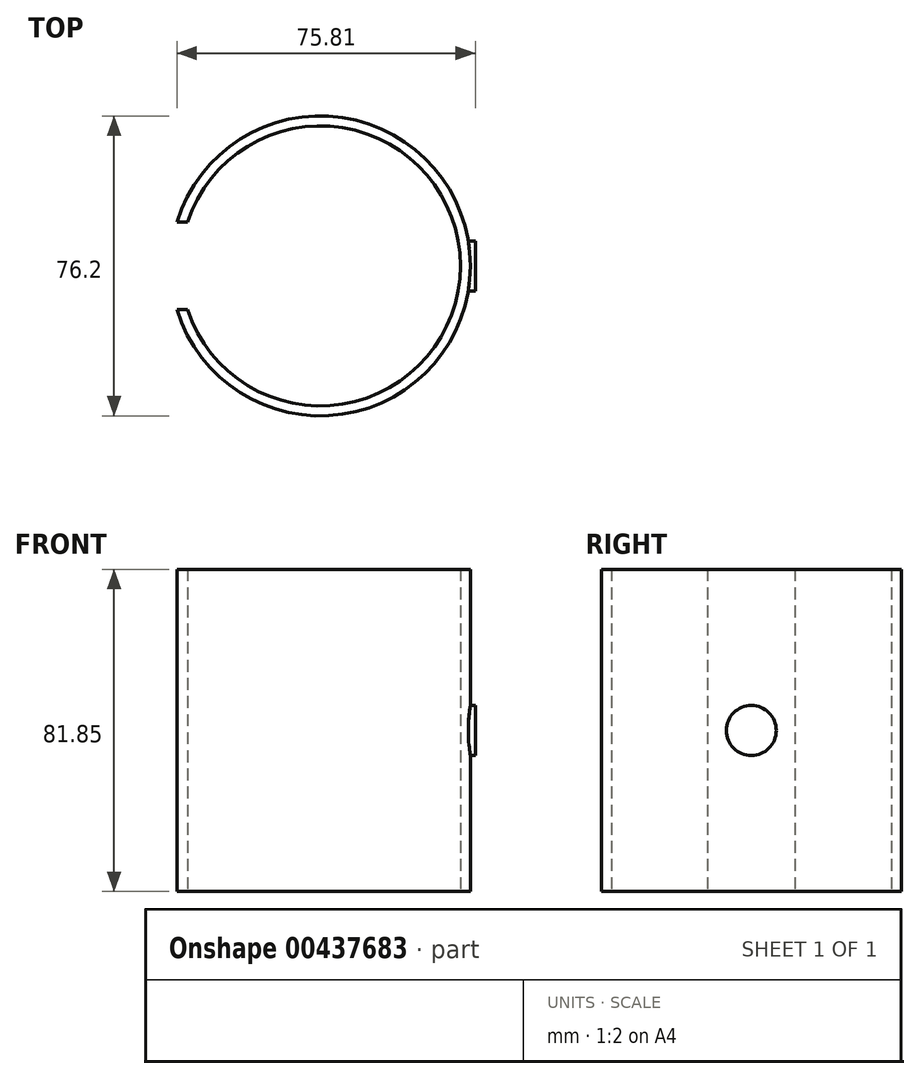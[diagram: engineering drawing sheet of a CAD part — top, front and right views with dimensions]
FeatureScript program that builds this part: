
annotation { "Feature Type Name" : "Feature", "Feature Type Description" : "" }
export const myFeature = defineFeature(function(context is Context, id is Id, definition is map)
    precondition{}
    {
        {
            var Q0;
            Q0=qCreatedBy(makeId("Top.planeOp"),FACE);
            var sketch = newSketch(context, id + "F0", { "sketchPlane" : qUnion([Q0])});
            skCircle(sketch, "E0", {"center": v(0, 0) * mm, "radius": 38.1 * mm});
            skLineSegment(sketch, "E1.bottom", {"start": v(-36.44, 11.1) * mm, "end": v(36.44, 11.1) * mm});
            skLineSegment(sketch, "E1.top", {"start": v(-36.44, -11.1) * mm, "end": v(36.44, -11.1) * mm});
            skLineSegment(sketch, "E1.left", {"start": v(-36.44, 11.1) * mm, "end": v(-36.44, -11.1) * mm});
            skLineSegment(sketch, "E1.right", {"start": v(36.44, 11.1) * mm, "end": v(36.44, -11.1) * mm});
            skCircle(sketch, "E2", {"center": v(0, 0) * mm, "radius": 35.56 * mm});
            skSolve(sketch);
        }
        {
            var Q0;
            {var subQ0=sQuery(id+"F0.wireOp",EDGE,"E1.bottom");var subQ4=sQuery(id+"F0.wireOp",EDGE,"E2");var subQ5=makeQuery(id+"F0.imprint","INTERSECT",VERTEX,{"disambiguationData":[OD(0.0)],"derivedFrom":[subQ0,subQ4]});Q0=makeQuery(id+"F0.imprint","IMPRINT",FACE,{"disambiguationData":[TD([[makeQuery(id+"F0.imprint","IMPRINT",EDGE,{"disambiguationData":[TD([[subQ5,1.0]])],"derivedFrom":subQ4}),-1.0]])]});}
            var Q1;
            {var subQ0=sQuery(id+"F0.wireOp",EDGE,"E1.top");var subQ4=sQuery(id+"F0.wireOp",EDGE,"E2");var subQ5=makeQuery(id+"F0.imprint","INTERSECT",VERTEX,{"disambiguationData":[OD(0.0)],"derivedFrom":[subQ0,subQ4]});Q1=makeQuery(id+"F0.imprint","IMPRINT",FACE,{"disambiguationData":[TD([[makeQuery(id+"F0.imprint","IMPRINT",EDGE,{"disambiguationData":[TD([[subQ5,-1.0]])],"derivedFrom":subQ4}),-1.0]])]});}
            var Q2;
            {var subQ0=sQuery(id+"F0.wireOp",EDGE,"E1.right");Q2=makeQuery(id+"F0.imprint","IMPRINT",FACE,{"disambiguationData":[TD([[makeQuery(id+"F0.imprint","IMPRINT",EDGE,{"derivedFrom":subQ0}),-1.0]])]});}
            var Q3;
            {var subQ0=sQuery(id+"F0.wireOp",EDGE,"E1.right");Q3=makeQuery(id+"F0.imprint","IMPRINT",FACE,{"disambiguationData":[TD([[makeQuery(id+"F0.imprint","IMPRINT",EDGE,{"derivedFrom":subQ0}),1.0]])]});}
            var Q4;
            Q4 = qSketchRegion(id + "F2", true);
            extrude(context, id + "F1", {"entities" : qUnion([Q0, Q1, Q2, Q3, Q4]), "depth" : 81.85 * mm});
        }
        {
            var Q0;
            Q0=qCreatedBy(makeId("Right.planeOp"),FACE);
            var sketch = newSketch(context, id + "F2", { "sketchPlane" : qUnion([Q0])});
            skCircle(sketch, "E3", {"center": v(0, 40.93) * mm, "radius": 6.35 * mm});
            skSolve(sketch);
        }
        {
            var Q0;
            Q0=makeQuery(id+"F2.imprint","IMPRINT",FACE,{"disambiguationData":[TD([[makeQuery(id+"F2.imprint","IMPRINT",EDGE,{"derivedFrom":sQuery(id+"F2.wireOp",EDGE,"E3")}),1.0]])]});
            extrude(context, id + "F3", {"entities" : qUnion([Q0]), "operationType" : NewBodyOperationType.ADD, "depth" : 39.37 * mm});
        }
        {
            var Q0;
            Q0=qCreatedBy(makeId("Top.planeOp"),FACE);
            var sketch = newSketch(context, id + "F4", { "sketchPlane" : qUnion([Q0])});
            skCircle(sketch, "E4", {"center": v(0, 0) * mm, "radius": 35.56 * mm});
            skSolve(sketch);
        }
        {
            var Q0;
            Q0=makeQuery(id+"F4.imprint","IMPRINT",FACE,{"disambiguationData":[TD([[makeQuery(id+"F4.imprint","IMPRINT",EDGE,{"derivedFrom":sQuery(id+"F4.wireOp",EDGE,"E4")}),1.0]])]});
            extrude(context, id + "F5", {"entities" : qUnion([Q0]), "operationType" : NewBodyOperationType.REMOVE, "depth" : 215.9 * mm, "symmetric" : true});
        }
    });
